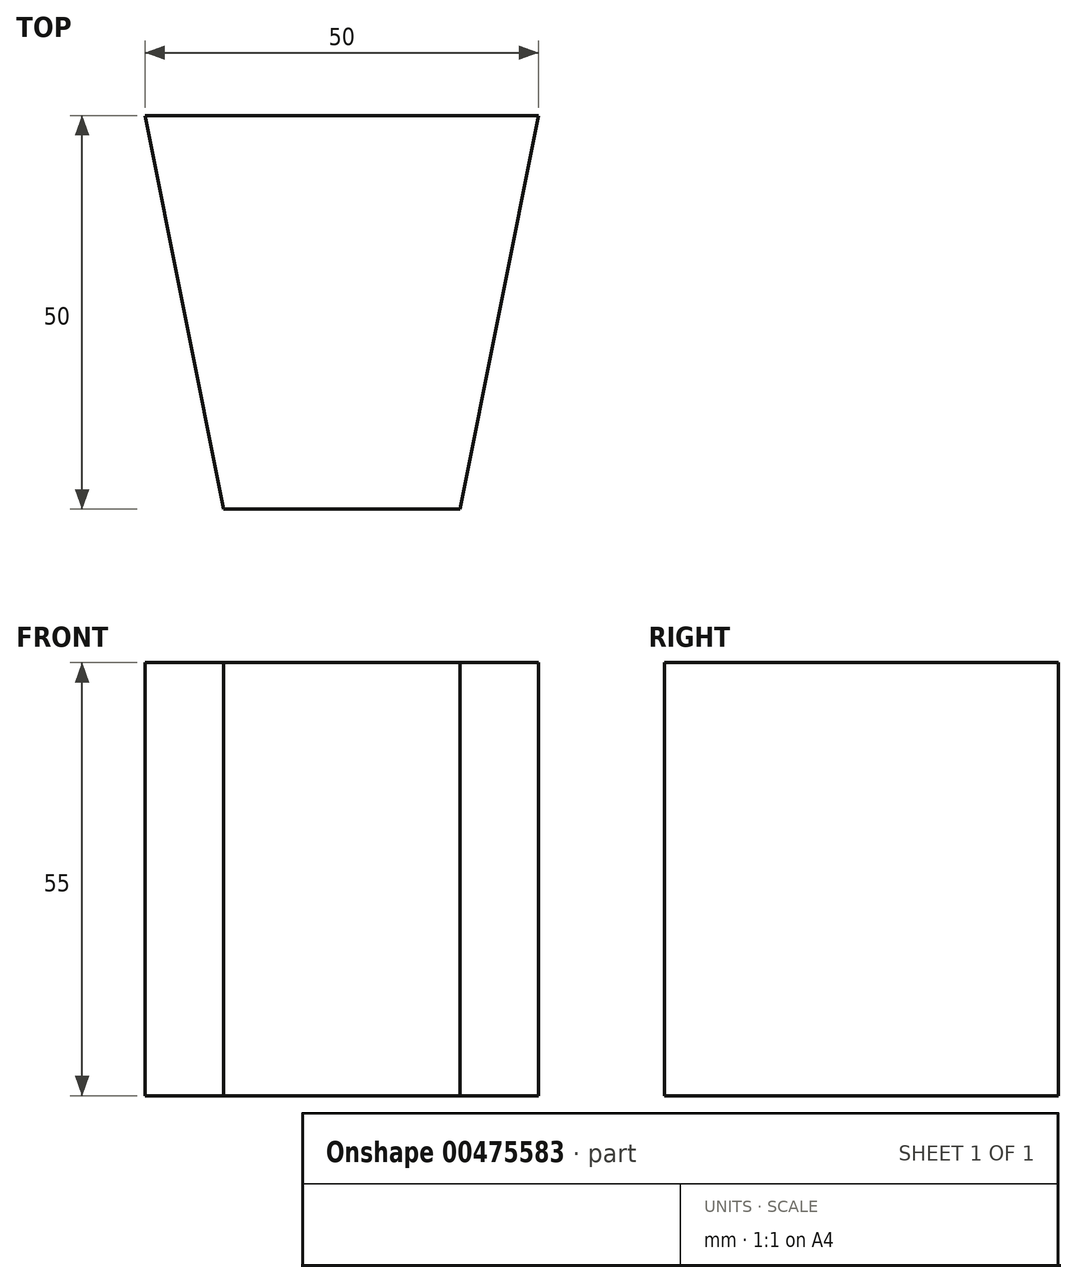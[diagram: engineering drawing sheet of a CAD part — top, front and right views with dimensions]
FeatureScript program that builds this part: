
annotation { "Feature Type Name" : "Feature", "Feature Type Description" : "" }
export const myFeature = defineFeature(function(context is Context, id is Id, definition is map)
    precondition{}
    {
        {
            var Q0;
            Q0=qCreatedBy(makeId("Top.planeOp"),FACE);
            var sketch = newSketch(context, id + "F0", { "sketchPlane" : qUnion([Q0])});
            skLineSegment(sketch, "E0", {"start": v(-15, -25) * mm, "end": v(15, -25) * mm});
            skLineSegment(sketch, "E1", {"start": v(15, -25) * mm, "end": v(25, 25) * mm});
            skLineSegment(sketch, "E2", {"start": v(25, 25) * mm, "end": v(-25, 25) * mm});
            skLineSegment(sketch, "E3", {"start": v(-25, 25) * mm, "end": v(-15, -25) * mm});
            skSolve(sketch);
        }
        {
            var Q0;
            Q0 = qSketchRegion(id + "F0", true);
            extrude(context, id + "F1", {"entities" : qUnion([Q0]), "depth" : 55 * mm});
        }
    });
